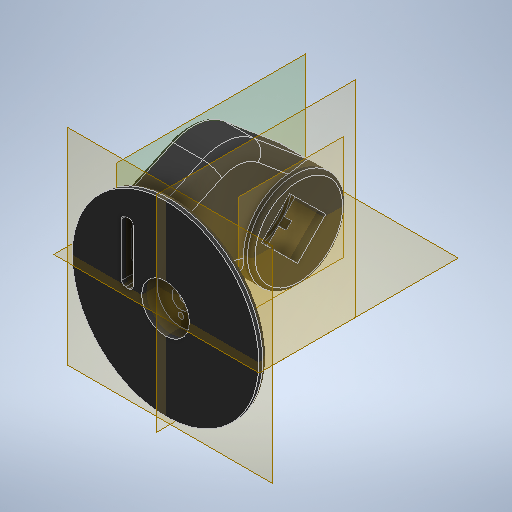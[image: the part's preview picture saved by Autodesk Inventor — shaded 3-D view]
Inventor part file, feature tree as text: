
AUTODESK INVENTOR PART (.ipt)
format: ipt  version: 2025.2 (Build 292293000, 293)  size: 595,968 bytes
history: native  units: mm
features: extrude x18, sketch x17, projected_geometry x6, fillet x5, plane x2, revolve x1, chamfer x1
ambient origin geometry x8: Origin, YZ Plane, XZ Plane, XY Plane, X Axis, Y Axis, Z Axis, Center Point
bodies: Body1 (feature_tree), Body2 (feature_tree)
feature tree (50):
  extrude  "Extrusion6"  Depth=5.0mm TaperAngle=0.0deg
  extrude  "Extrusion15"  Depth=35.0mm
  extrude  "Extrusion16"  Depth=8.1mm TaperAngle=0.0deg
  extrude  "Extrusion17"  Depth=3.0mm
  revolve  "Revolution2"  [1 undecoded]
  fillet  "Fillet8"  Radius=4.75mm
  extrude  "Extrusion18"  Depth=3.0mm
  plane  "Work Plane5"
  extrude  "Extrusion19"  Depth=65.0mm
  extrude  "Extrusion20"  [1 undecoded]
  extrude  "Extrusion21"  Depth=10.0mm TaperAngle=0.0deg
  extrude  "Extrusion22"  Depth=35.0mm
  extrude  "Extrusion23"  Depth=20.071286mm
  extrude  "Extrusion24"  Depth=10.0mm TaperAngle=0.0deg
  extrude  "Extrusion25"  Depth=15.0mm
  extrude  "Extrusion26"  Depth=10.0mm
  sketch  "Sketch30"  dims[d126=42.0mm d128=36.0mm]
  extrude  "Extrusion27"  Depth=36.0mm
  extrude  "Extrusion28"  Depth=15.0mm
  plane  "Work Plane6"
  extrude  "Extrusion29"  Depth=2.0mm
  fillet  "Fillet9"  Radius=21.0mm
  chamfer  "Chamfer2"  Distance=7.9mm
  fillet  "Fillet10"  Radius=11.0mm
  fillet  "Fillet11"  Radius=10.0mm
  sketch  "Sketch32"  dims[d132=12.5mm d133=0.0mm d135=41.0mm d136=21.0mm d137=7.9mm d138=11.0mm d139=10.0mm d140=0.0mm d141=14.253mm d142=0.0mm d143=0.0mm d144=10.0mm d145=2.6mm d146=3.5mm d147=4.0mm d148=7.5mm d149=4.0mm d150=0.0mm d151=7.5mm d152=0.0mm d153=-2.5mm d154=2.5mm d155=2.0mm d156=0.0mm d157=5.6mm d158=2.0mm d159=45.0deg d160=7.0mm d161=2.0mm d162=7.0mm d165=1.0mm d166=32.0mm d167=0.0mm d168=0.0mm d169=15.0mm d170=0.0mm d171=2.0mm d134=0.5mm]
  extrude  "Extrusion30"  Depth=2.0mm
  extrude  "Extrusion31"  TaperAngle=0.0deg  [1 undecoded]
  fillet  "Fillet12"  Radius=10.0mm
  sketch  "Sketch8"  dims[d28=98.0mm d30=5.0mm d31=0.0mm]
  sketch  "Sketch16"  dims[d90=5.6mm d91=0.0mm d92=35.0mm]
  sketch  "Sketch17"  dims[d93=25.0mm d94=8.1mm d95=0.0mm]
  sketch  "Sketch18"  dims[d96=7.0mm d97=3.0mm]
  sketch  "Sketch19"  dims[d98=14.5mm d99=8.1mm d100=0.0mm d101=4.75mm]
  sketch  "Sketch20"  dims[d102=90.0deg d103=3.0mm]
  sketch  "Sketch21"  dims[d104=50.0mm d105=65.0mm]
  sketch  "Sketch22"  dims[d106=28.5mm d107=0.0mm d108=-4.0mm]
  projected_geometry  "Projected Loop2"
  sketch  "Sketch23"  dims[d109=28.5mm d110=0.0mm d111=10.0mm d112=0.0mm]
  sketch  "Sketch25"  dims[d113=8.726646mm d114=35.0mm]
  projected_geometry  "Projected Loop3"
  sketch  "Sketch26"  dims[d115=25.0mm d116=20.071286mm]
  projected_geometry  "Projected Loop4"
  sketch  "Sketch27"  dims[d117=10.0mm d118=0.0mm d119=10.0mm d120=0.0mm]
  projected_geometry  "Projected Loop5"
  sketch  "Sketch28"  dims[d121=11.34464mm d122=15.0mm]
  projected_geometry  "Projected Loop6"
  sketch  "Sketch29"  dims[d123=10.0mm d124=0.0mm d125=41.0mm]
  projected_geometry  "Projected Loop7"
  sketch  "Sketch31"  dims[d129=17.0mm d131=15.0mm]
note: 3 required parameter values undecoded (feature->parameter linkage not recoverable at this tier; creation-order binding heuristic only, values carry confidence <= 0.55)